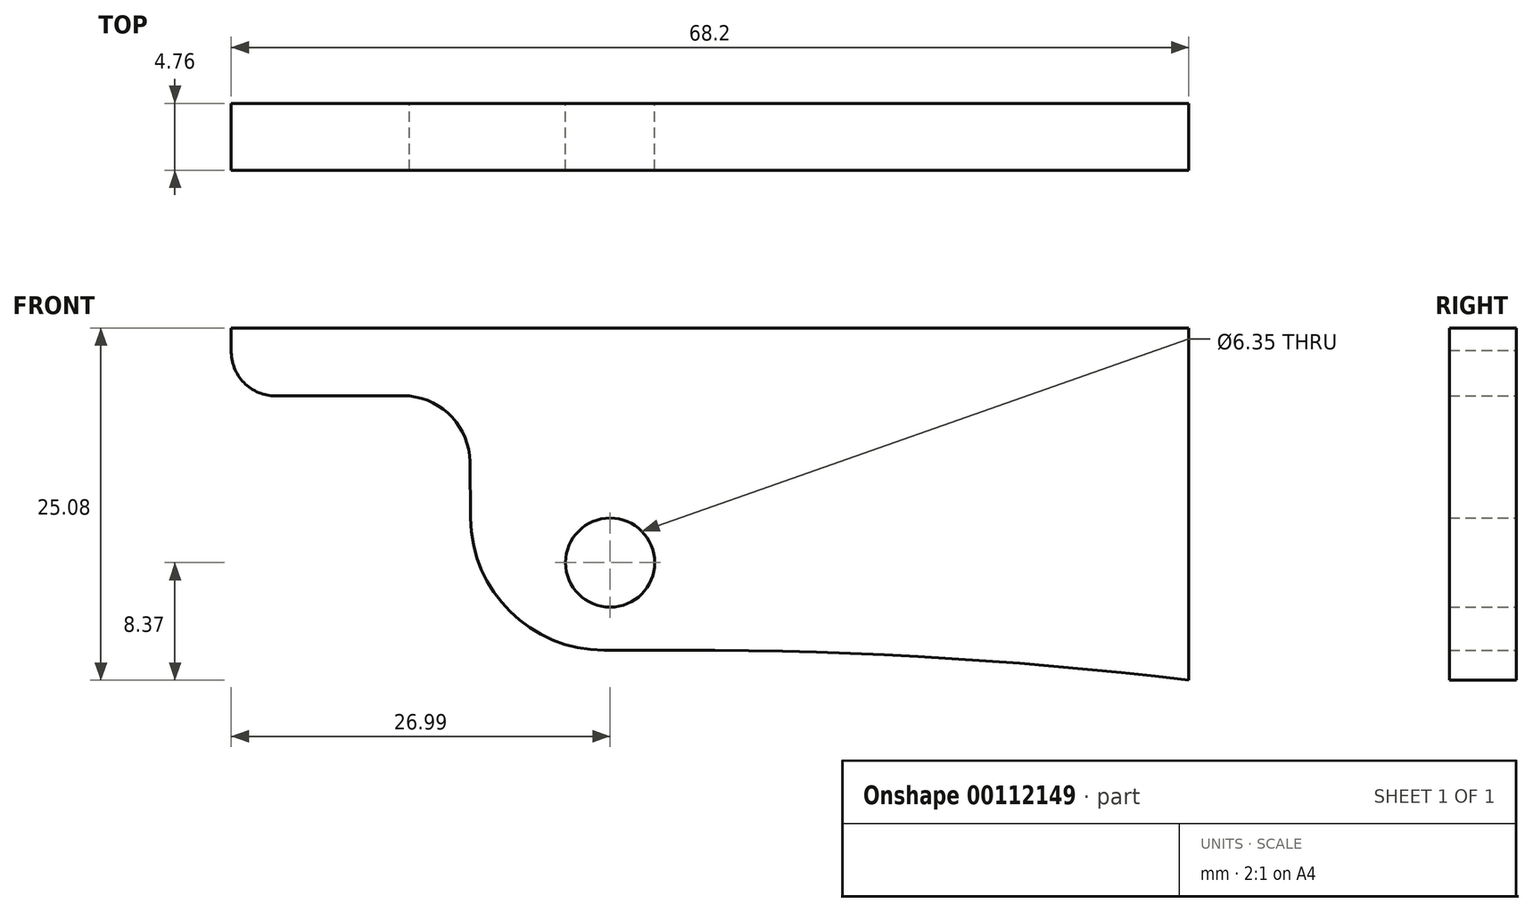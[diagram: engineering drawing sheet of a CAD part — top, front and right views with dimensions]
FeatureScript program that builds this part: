
annotation { "Feature Type Name" : "Feature", "Feature Type Description" : "" }
export const myFeature = defineFeature(function(context is Context, id is Id, definition is map)
    precondition{}
    {
        {
            var Q0;
            Q0=qCreatedBy(makeId("Front.planeOp"),FACE);
            var sketch = newSketch(context, id + "F0", { "sketchPlane" : qUnion([Q0])});
            skCircle(sketch, "E0", {"center": v(0, 0) * mm, "radius": 3.18 * mm});
            skLineSegment(sketch, "E1", {"start": v(-26.99, 16.71) * mm, "end": v(41.21, 16.71) * mm});
            skLineSegment(sketch, "E2", {"start": v(41.21, 16.71) * mm, "end": v(41.21, -8.37) * mm});
            skArc(sketch, "E3", {"start": v(41.21, -8.37) * mm, "mid": v(21.94, -6.69) * mm, "end": v(2.6, -6.24) * mm});
            skLineSegment(sketch, "E4", {"start": v(2.6, -6.24) * mm, "end": v(-0.43, -6.24) * mm});
            skArc(sketch, "E5", {"start": v(-9.95, 3.17) * mm, "mid": v(-7.12, -3.49) * mm, "end": v(-0.43, -6.24) * mm});
            skLineSegment(sketch, "E6", {"start": v(-9.95, 3.18) * mm, "end": v(-10, 7.19) * mm});
            skArc(sketch, "E7", {"start": v(-10, 7.19) * mm, "mid": v(-11.25, 10.35) * mm, "end": v(-14.29, 11.87) * mm});
            skLineSegment(sketch, "E8", {"start": v(-14.29, 11.87) * mm, "end": v(-23.81, 11.87) * mm});
            skLineSegment(sketch, "E9", {"start": v(-26.99, 16.71) * mm, "end": v(-26.99, 15.13) * mm});
            skArc(sketch, "E10", {"start": v(-26.99, 15.13) * mm, "mid": v(-26.09, 12.83) * mm, "end": v(-23.81, 11.87) * mm});
            skSolve(sketch);
        }
        {
            var Q0;
            Q0=makeQuery(id+"F0.imprint","IMPRINT",FACE,{"disambiguationData":[TD([[makeQuery(id+"F0.imprint","IMPRINT",EDGE,{"derivedFrom":sQuery(id+"F0.wireOp",EDGE,"E0")}),-1.0]])]});
            extrude(context, id + "F1", {"entities" : qUnion([Q0]), "depth" : 4.76 * mm});
        }
    });
